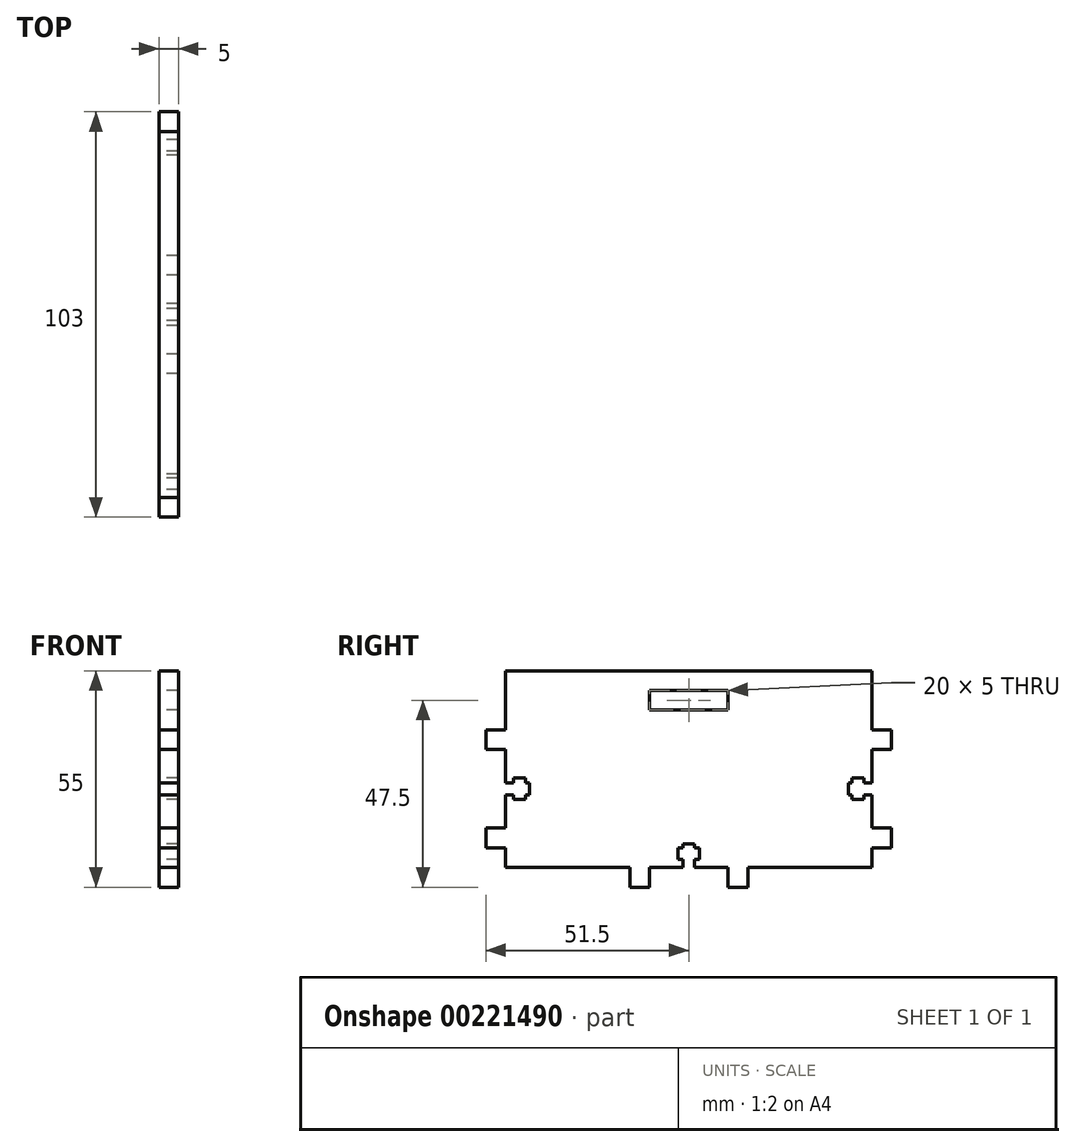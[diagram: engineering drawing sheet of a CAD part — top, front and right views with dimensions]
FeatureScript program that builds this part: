
annotation { "Feature Type Name" : "Feature", "Feature Type Description" : "" }
export const myFeature = defineFeature(function(context is Context, id is Id, definition is map)
    precondition{}
    {
        {
            assignVariable(context, id + "F0", {"name" : "thickness", "anyValue" : 5});
        }
        {
            var Q0;
            Q0=qCreatedBy(makeId("Right.planeOp"),FACE);
            var sketch = newSketch(context, id + "F1", { "sketchPlane" : qUnion([Q0])});
            skLineSegment(sketch, "E0.bottom", {"start": v(0, 0) * mm, "end": v(31.5, 0) * mm});
            skLineSegment(sketch, "E0.top", {"start": v(0, 40) * mm, "end": v(31.5, 40) * mm, "construction": true});
            skLineSegment(sketch, "E0.left", {"start": v(0, 0) * mm, "end": v(0, 5) * mm});
            skLineSegment(sketch, "E0.right", {"start": v(93, 0) * mm, "end": v(93, 5) * mm});
            skLineSegment(sketch, "E1.0", {"start": v(-5, -5) * mm, "end": v(-5, 45) * mm, "construction": true});
            skLineSegment(sketch, "E1.1", {"start": v(-5, -5) * mm, "end": v(98, -5) * mm, "construction": true});
            skLineSegment(sketch, "E1.2", {"start": v(98, -5) * mm, "end": v(98, 45) * mm, "construction": true});
            skLineSegment(sketch, "E1.3", {"start": v(-5, 45) * mm, "end": v(98, 45) * mm, "construction": true});
            skLineSegment(sketch, "E2", {"start": v(0, 35) * mm, "end": v(-5, 35) * mm});
            skLineSegment(sketch, "E3", {"start": v(-5, 35) * mm, "end": v(-5, 30) * mm});
            skLineSegment(sketch, "E4", {"start": v(-5, 30) * mm, "end": v(0, 30) * mm});
            skLineSegment(sketch, "E5", {"start": v(0, 10) * mm, "end": v(-5, 10) * mm});
            skLineSegment(sketch, "E6", {"start": v(-5, 10) * mm, "end": v(-5, 5) * mm});
            skLineSegment(sketch, "E7", {"start": v(-5, 5) * mm, "end": v(0, 5) * mm});
            skLineSegment(sketch, "E8", {"start": v(0, 21.5) * mm, "end": v(2, 21.5) * mm});
            skLineSegment(sketch, "E9", {"start": v(2, 21.5) * mm, "end": v(2, 22.75) * mm});
            skLineSegment(sketch, "E10", {"start": v(2, 22.75) * mm, "end": v(5, 22.75) * mm});
            skLineSegment(sketch, "E11", {"start": v(5, 22.75) * mm, "end": v(5, 21.5) * mm});
            skLineSegment(sketch, "E12", {"start": v(5, 21.5) * mm, "end": v(6, 21.5) * mm});
            skLineSegment(sketch, "E13", {"start": v(6, 21.5) * mm, "end": v(6, 18.5) * mm});
            skLineSegment(sketch, "E14", {"start": v(6, 18.5) * mm, "end": v(5, 18.5) * mm});
            skLineSegment(sketch, "E15", {"start": v(5, 18.5) * mm, "end": v(5, 17.25) * mm});
            skLineSegment(sketch, "E16", {"start": v(5, 17.25) * mm, "end": v(2, 17.25) * mm});
            skLineSegment(sketch, "E17", {"start": v(2, 17.25) * mm, "end": v(2, 18.5) * mm});
            skLineSegment(sketch, "E18", {"start": v(2, 18.5) * mm, "end": v(0, 18.5) * mm});
            skPoint(sketch, "E19", {"position": v(6, 20) * mm});
            skLineSegment(sketch, "E20.trimOffspring", {"start": v(0, 18.5) * mm, "end": v(0, 10) * mm});
            skPoint(sketch, "E21", {"position": v(0, 20) * mm});
            skLineSegment(sketch, "E22", {"start": v(46.5, 45) * mm, "end": v(46.5, -5) * mm, "construction": true});
            skLineSegment(sketch, "E23", {"start": v(0, 20) * mm, "end": v(93, 20) * mm, "construction": true});
            skLineSegment(sketch, "E24.MirrorCS", {"start": v(91, 18.5) * mm, "end": v(93, 18.5) * mm});
            skLineSegment(sketch, "E25.MirrorCS", {"start": v(88, 18.5) * mm, "end": v(88, 17.25) * mm});
            skLineSegment(sketch, "E26.MirrorCS", {"start": v(88, 22.75) * mm, "end": v(88, 21.5) * mm});
            skLineSegment(sketch, "E27.MirrorCS", {"start": v(93, 21.5) * mm, "end": v(91, 21.5) * mm});
            skLineSegment(sketch, "E28.MirrorCS", {"start": v(91, 21.5) * mm, "end": v(91, 22.75) * mm});
            skLineSegment(sketch, "E29.MirrorCS", {"start": v(91, 17.25) * mm, "end": v(91, 18.5) * mm});
            skLineSegment(sketch, "E30.MirrorCS", {"start": v(88, 21.5) * mm, "end": v(87, 21.5) * mm});
            skLineSegment(sketch, "E31.MirrorCS", {"start": v(87, 18.5) * mm, "end": v(88, 18.5) * mm});
            skLineSegment(sketch, "E32.MirrorCS", {"start": v(87, 21.5) * mm, "end": v(87, 18.5) * mm});
            skLineSegment(sketch, "E33.MirrorCS", {"start": v(91, 22.75) * mm, "end": v(88, 22.75) * mm});
            skLineSegment(sketch, "E34.MirrorCS", {"start": v(93, 18.5) * mm, "end": v(93, 10) * mm});
            skPoint(sketch, "E35.MirrorP", {"position": v(87, 20) * mm});
            skLineSegment(sketch, "E36.MirrorCS", {"start": v(98, 5) * mm, "end": v(93, 5) * mm});
            skLineSegment(sketch, "E37.MirrorCS", {"start": v(93, 10) * mm, "end": v(98, 10) * mm});
            skLineSegment(sketch, "E38.MirrorCS", {"start": v(98, 30) * mm, "end": v(93, 30) * mm});
            skLineSegment(sketch, "E39.MirrorCS", {"start": v(98, 35) * mm, "end": v(98, 30) * mm});
            skLineSegment(sketch, "E40.MirrorCS", {"start": v(98, 10) * mm, "end": v(98, 5) * mm});
            skLineSegment(sketch, "E41.MirrorCS", {"start": v(93, 35) * mm, "end": v(98, 35) * mm});
            skPoint(sketch, "E42.MirrorP", {"position": v(93, 20) * mm});
            skLineSegment(sketch, "E43.MirrorCS", {"start": v(88, 17.25) * mm, "end": v(91, 17.25) * mm});
            skLineSegment(sketch, "E44.trimOffspring", {"start": v(0, 35) * mm, "end": v(0, 40) * mm});
            skLineSegment(sketch, "E45.trimOffspring", {"start": v(0, 21.5) * mm, "end": v(0, 30) * mm});
            skLineSegment(sketch, "E46.trimOffspring", {"start": v(0, 10) * mm, "end": v(0, 18.5) * mm});
            skLineSegment(sketch, "E47.trimOffspring", {"start": v(93, 21.5) * mm, "end": v(93, 30) * mm});
            skLineSegment(sketch, "E48.trimOffspring", {"start": v(93, 35) * mm, "end": v(93, 40) * mm});
            skLineSegment(sketch, "E49.trimOffspring", {"start": v(93, 10) * mm, "end": v(93, 18.5) * mm});
            skLineSegment(sketch, "E50", {"start": v(61.5, 40) * mm, "end": v(61.5, 45) * mm, "construction": true});
            skLineSegment(sketch, "E51", {"start": v(61.5, 45) * mm, "end": v(56.5, 45) * mm, "construction": true});
            skLineSegment(sketch, "E52", {"start": v(56.5, 45) * mm, "end": v(56.5, 40) * mm});
            skLineSegment(sketch, "E53", {"start": v(36.5, 40) * mm, "end": v(36.5, 45) * mm});
            skLineSegment(sketch, "E54", {"start": v(36.5, 45) * mm, "end": v(31.5, 45) * mm, "construction": true});
            skLineSegment(sketch, "E55", {"start": v(31.5, 45) * mm, "end": v(31.5, 40) * mm, "construction": true});
            skLineSegment(sketch, "E56", {"start": v(48, 40) * mm, "end": v(48, 38) * mm, "construction": true});
            skLineSegment(sketch, "E57", {"start": v(48, 38) * mm, "end": v(49.25, 38) * mm, "construction": true});
            skLineSegment(sketch, "E58", {"start": v(49.25, 38) * mm, "end": v(49.25, 35) * mm, "construction": true});
            skLineSegment(sketch, "E59", {"start": v(49.25, 35) * mm, "end": v(48, 35) * mm, "construction": true});
            skLineSegment(sketch, "E60", {"start": v(48, 35) * mm, "end": v(48, 34) * mm, "construction": true});
            skLineSegment(sketch, "E61", {"start": v(48, 34) * mm, "end": v(45, 34) * mm, "construction": true});
            skLineSegment(sketch, "E62", {"start": v(45, 34) * mm, "end": v(45, 35) * mm, "construction": true});
            skLineSegment(sketch, "E63", {"start": v(45, 35) * mm, "end": v(43.75, 35) * mm, "construction": true});
            skLineSegment(sketch, "E64", {"start": v(43.75, 35) * mm, "end": v(43.75, 38) * mm, "construction": true});
            skLineSegment(sketch, "E65", {"start": v(43.75, 38) * mm, "end": v(45, 38) * mm, "construction": true});
            skLineSegment(sketch, "E66", {"start": v(45, 38) * mm, "end": v(45, 40) * mm, "construction": true});
            skPoint(sketch, "E67", {"position": v(46.5, 34) * mm});
            skLineSegment(sketch, "E68.trimOffspring", {"start": v(56.5, 40) * mm, "end": v(48, 40) * mm, "construction": true});
            skLineSegment(sketch, "E69.trimOffspring", {"start": v(45, 40) * mm, "end": v(36.5, 40) * mm, "construction": true});
            skLineSegment(sketch, "E70.trimOffspring", {"start": v(48, 40) * mm, "end": v(56.5, 40) * mm, "construction": true});
            skLineSegment(sketch, "E71.trimOffspring", {"start": v(36.5, 40) * mm, "end": v(45, 40) * mm});
            skPoint(sketch, "E72", {"position": v(46.5, 40) * mm});
            skLineSegment(sketch, "E73.trimOffspring", {"start": v(61.5, 40) * mm, "end": v(93, 40) * mm, "construction": true});
            skLineSegment(sketch, "E74.MirrorCS", {"start": v(45, 6) * mm, "end": v(45, 5) * mm});
            skLineSegment(sketch, "E75.MirrorCS", {"start": v(48, 5) * mm, "end": v(48, 6) * mm});
            skLineSegment(sketch, "E76.MirrorCS", {"start": v(48, 0) * mm, "end": v(56.5, 0) * mm});
            skLineSegment(sketch, "E77.MirrorCS", {"start": v(45, 5) * mm, "end": v(43.75, 5) * mm});
            skLineSegment(sketch, "E78.MirrorCS", {"start": v(43.75, 2) * mm, "end": v(45, 2) * mm});
            skLineSegment(sketch, "E79.MirrorCS", {"start": v(45, 2) * mm, "end": v(45, 0) * mm});
            skLineSegment(sketch, "E80.MirrorCS", {"start": v(49.25, 5) * mm, "end": v(48, 5) * mm});
            skLineSegment(sketch, "E81.MirrorCS", {"start": v(48, 0) * mm, "end": v(48, 2) * mm});
            skLineSegment(sketch, "E82.MirrorCS", {"start": v(36.5, 0) * mm, "end": v(45, 0) * mm});
            skLineSegment(sketch, "E83.MirrorCS", {"start": v(48, 2) * mm, "end": v(49.25, 2) * mm});
            skLineSegment(sketch, "E84.MirrorCS", {"start": v(48, 6) * mm, "end": v(45, 6) * mm});
            skLineSegment(sketch, "E85.MirrorCS", {"start": v(56.5, 0) * mm, "end": v(48, 0) * mm});
            skLineSegment(sketch, "E86.MirrorCS", {"start": v(49.25, 2) * mm, "end": v(49.25, 5) * mm});
            skLineSegment(sketch, "E87.MirrorCS", {"start": v(36.5, 0) * mm, "end": v(36.5, -5) * mm});
            skPoint(sketch, "E88.MirrorP", {"position": v(46.5, 0) * mm});
            skLineSegment(sketch, "E89.MirrorCS", {"start": v(45, 0) * mm, "end": v(36.5, 0) * mm});
            skLineSegment(sketch, "E90.MirrorCS", {"start": v(56.5, -5) * mm, "end": v(56.5, 0) * mm});
            skPoint(sketch, "E91.MirrorP", {"position": v(46.5, 6) * mm});
            skLineSegment(sketch, "E92.MirrorCS", {"start": v(61.5, -5) * mm, "end": v(56.5, -5) * mm});
            skLineSegment(sketch, "E93.MirrorCS", {"start": v(36.5, -5) * mm, "end": v(31.5, -5) * mm});
            skLineSegment(sketch, "E94.MirrorCS", {"start": v(61.5, 0) * mm, "end": v(61.5, -5) * mm});
            skLineSegment(sketch, "E95.MirrorCS", {"start": v(31.5, -5) * mm, "end": v(31.5, 0) * mm});
            skLineSegment(sketch, "E96.MirrorCS", {"start": v(43.75, 5) * mm, "end": v(43.75, 2) * mm});
            skLineSegment(sketch, "E97.trimOffspring", {"start": v(61.5, 0) * mm, "end": v(93, 0) * mm});
            skLineSegment(sketch, "E98.trimOffspring", {"start": v(0, 30) * mm, "end": v(0, 21.5) * mm});
            skLineSegment(sketch, "E99.trimOffspring", {"start": v(93, 30) * mm, "end": v(93, 21.5) * mm});
            skLineSegment(sketch, "E100", {"start": v(0, 40) * mm, "end": v(0, 50) * mm});
            skLineSegment(sketch, "E101", {"start": v(0, 50) * mm, "end": v(93, 50) * mm});
            skLineSegment(sketch, "E102", {"start": v(93, 50) * mm, "end": v(93, 40) * mm});
            skLineSegment(sketch, "E103", {"start": v(36.5, 45) * mm, "end": v(56.5, 45) * mm});
            skLineSegment(sketch, "E104", {"start": v(36.5, 40) * mm, "end": v(56.5, 40) * mm});
            skSolve(sketch);
        }
        {
            var Q0;
            Q0=makeQuery(id+"F1.imprint","IMPRINT",FACE,{"disambiguationData":[TD([[makeQuery(id+"F1.imprint","IMPRINT",EDGE,{"derivedFrom":sQuery(id+"F1.wireOp",EDGE,"E0.bottom")}),1.0]])]});
            extrude(context, id + "F2", {"entities" : qUnion([Q0]), "depth" : (getVariable(context, 'thickness')) * mm});
        }
    });
